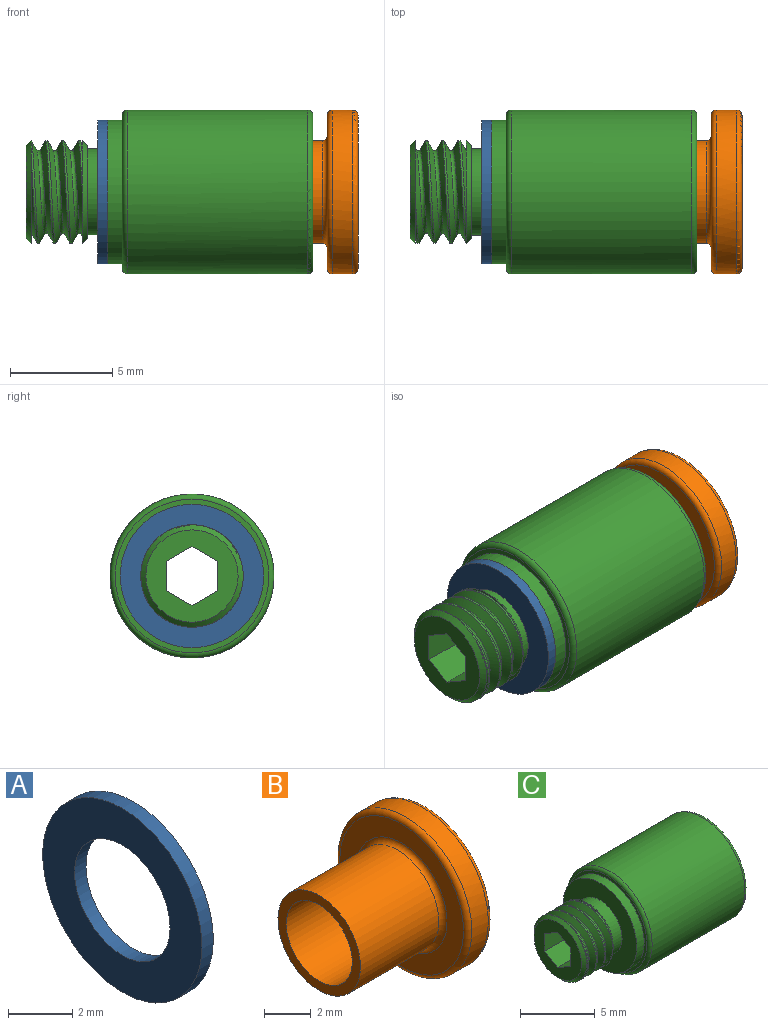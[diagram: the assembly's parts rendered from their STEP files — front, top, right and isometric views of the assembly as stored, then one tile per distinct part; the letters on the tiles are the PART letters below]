
ASSEMBLY  parts=3 mates=2
PART A: 4 faces, bbox 0.5x7x7 mm
  f0: cylinder r=3.5mm len=7mm, axis (1,0,0), area 11mm2, adj f2,f3
  f1: cylinder r=2.1mm len=4.2mm, axis (1,0,0), area 6.6mm2, adj f2,f3
  f2: plane 7x7mm, normal (-1,0,0), area 24.6mm2, adj f0,f1
  f3: plane 7x7mm, normal (1,0,0), area 24.6mm2, adj f0,f1
PART B: 9 faces, bbox 6.5x8.7x8.7 mm
  f0: cylinder r=2.5mm len=5mm, axis (1,0,0), area 74.6mm2, adj f1,f8
  f1: plane 5x5mm, normal (-1,0,0), area 7.1mm2, adj f0,f2
  f2: cylinder r=2mm len=6.5mm, axis (1,0,0), area 81.7mm2, adj f1,f3
  f3: plane 7.5x7.5mm, normal (1,0,0), area 31.6mm2, adj f2,f6
  f4: cylinder r=4mm len=8mm, axis (1,0,0), area 25.1mm2, adj f6,f7
  f5: plane 7.5x7.5mm, normal (-1,0,0), area 20.4mm2, adj f7,f8
  f6: torus R=3.75mm, axis (-1,0,0), area 9.6mm2, adj f3,f4
  f7: torus R=3.75mm, axis (1,0,0), area 9.6mm2, adj f4,f5
  f8: torus R=2.75mm, axis (1,0,0), area 6.4mm2, adj f0,f5
PART C: 28 faces, bbox 14.3x8.9x8.9 mm
  f0: cylinder r=2.5mm len=5mm, axis (-1,0,0), area 5mm2, adj f21,f22,f24,f25
  f1: plane 4.5x4.5mm, normal (-1,0,0), area 10.5mm2, adj f11,f12,f13,f14,f15,f16,f22
  f2: plane 4.5x4.5mm, normal (1,0,0), area 10.5mm2, adj f11,f12,f13,f14,f15,f16,f17
  f3: cylinder r=2.5mm len=7.8mm, axis (-1,0,0), area 122.5mm2, adj f17,f18
  f4: plane 7.5x7.5mm, normal (1,0,0), area 20.4mm2, adj f18,f19
  f5: cylinder r=4mm len=8.8mm, axis (-1,0,0), area 221.2mm2, adj f19,f20
  f6: plane 7.5x7.5mm, normal (-1,0,0), area 5.7mm2, adj f7,f20
  f7: cylinder r=3.5mm len=7mm, axis (-1,0,0), area 15.4mm2, adj f6,f8
  f8: plane 7x7mm, normal (-1,0,0), area 24.6mm2, adj f7,f9
  f9: cylinder r=2.1mm len=4.2mm, axis (-1,0,0), area 13.2mm2, adj f8,f10
  f10: plane 4.5x4.5mm, normal (1,0,0), area 2mm2, adj f9,f21
  f11: plane 5.7x1.44mm, normal (0,1,0), area 8.2mm2, adj f1,f2,f12,f16
  f12: plane 5.7x1.25mm, normal (0,0.5,-0.87), area 8.2mm2, adj f1,f2,f11,f13
  f13: plane 5.7x1.25mm, normal (0,-0.5,-0.87), area 8.2mm2, adj f1,f2,f12,f14
  f14: plane 5.7x1.44mm, normal (0,-1,0), area 8.2mm2, adj f1,f2,f13,f15
  f15: plane 5.7x1.25mm, normal (0,-0.5,0.87), area 8.2mm2, adj f1,f2,f14,f16
  f16: plane 5.7x1.25mm, normal (0,0.5,0.87), area 8.2mm2, adj f1,f2,f11,f15
  f17: torus R=2.25mm, axis (1,0,0), area 5.9mm2, adj f2,f3
  f18: torus R=2.75mm, axis (1,0,0), area 6.4mm2, adj f3,f4
  f19: torus R=3.75mm, axis (1,0,0), area 9.6mm2, adj f4,f5
  f20: torus R=3.75mm, axis (-1,0,0), area 9.6mm2, adj f5,f6
  f21: cone r=2.5mm half-angle=45deg, axis (-1,0,0), area 5.3mm2, adj f0,f10,f26
  f22: cone r=2.25mm half-angle=45deg, axis (1,0,0), area 5.3mm2, adj f0,f1,f27
  f23: bspline ~4.77x4.13mm, area 9mm2, adj f24,f25,f26,f27
  f24: bspline ~5.77x5mm, area 22.5mm2, adj f0,f23,f26,f27
  f25: bspline ~5.77x5mm, area 22.4mm2, adj f0,f23,f26,f27
  f26: plane 5.23x5.23mm, normal (-1,0,0), area 3.7mm2, adj f21,f23,f24,f25
  f27: plane 5.22x5.22mm, normal (1,0,0), area 3.7mm2, adj f22,f23,f24,f25
PLACE A at identity
PLACE B at identity
PLACE C at identity fixed
MATE fastened C.f0 <-> A.f0  axis (-1,0,0) through (-1.7,0,0)mm
MATE fastened B.f7 <-> C.f0  axis (-1,0,0) through (4,0,0)mm
